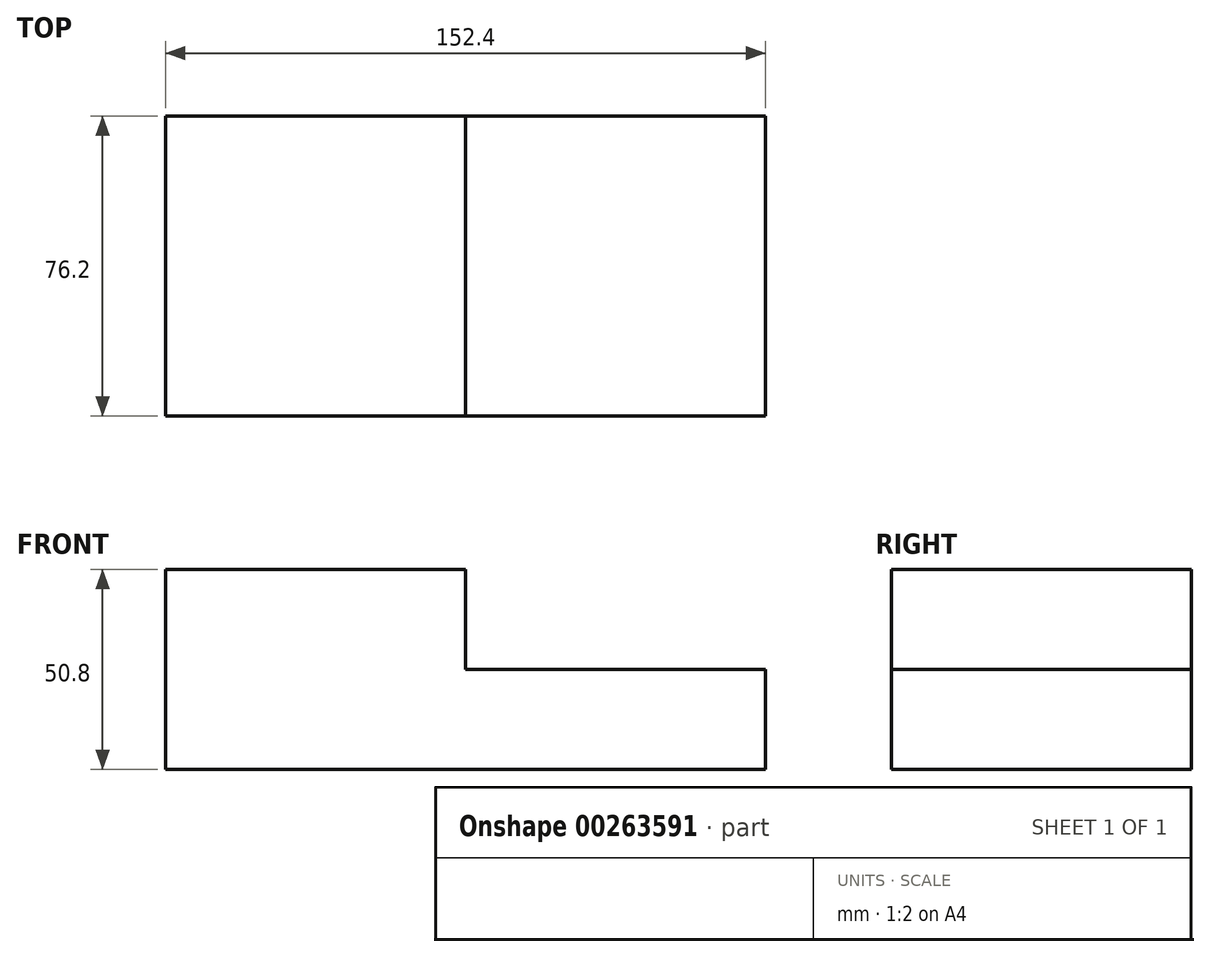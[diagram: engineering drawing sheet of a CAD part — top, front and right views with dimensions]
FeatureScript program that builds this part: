
annotation { "Feature Type Name" : "Feature", "Feature Type Description" : "" }
export const myFeature = defineFeature(function(context is Context, id is Id, definition is map)
    precondition{}
    {
        {
            var Q0;
            Q0=qCreatedBy(makeId("Front.planeOp"),FACE);
            var sketch = newSketch(context, id + "F0", { "sketchPlane" : qUnion([Q0])});
            skLineSegment(sketch, "E0", {"start": v(-76.11, 0) * mm, "end": v(76.29, 0) * mm});
            skLineSegment(sketch, "E1", {"start": v(-76.11, 0) * mm, "end": v(-76.11, 50.8) * mm});
            skLineSegment(sketch, "E2", {"start": v(-76.11, 50.8) * mm, "end": v(0.09, 50.8) * mm});
            skLineSegment(sketch, "E3", {"start": v(0.09, 50.8) * mm, "end": v(0.09, 25.4) * mm});
            skLineSegment(sketch, "E4", {"start": v(0.09, 25.4) * mm, "end": v(76.29, 25.4) * mm});
            skLineSegment(sketch, "E5", {"start": v(76.29, 25.4) * mm, "end": v(76.29, 0) * mm});
            skSolve(sketch);
        }
        {
            var Q0;
            Q0=makeQuery(id+"F0.imprint","IMPRINT",FACE,{"disambiguationData":[TD([[makeQuery(id+"F0.imprint","IMPRINT",EDGE,{"derivedFrom":sQuery(id+"F0.wireOp",EDGE,"E0")}),1.0]])]});
            extrude(context, id + "F1", {"entities" : qUnion([Q0]), "depth" : 76.2 * mm});
        }
    });
